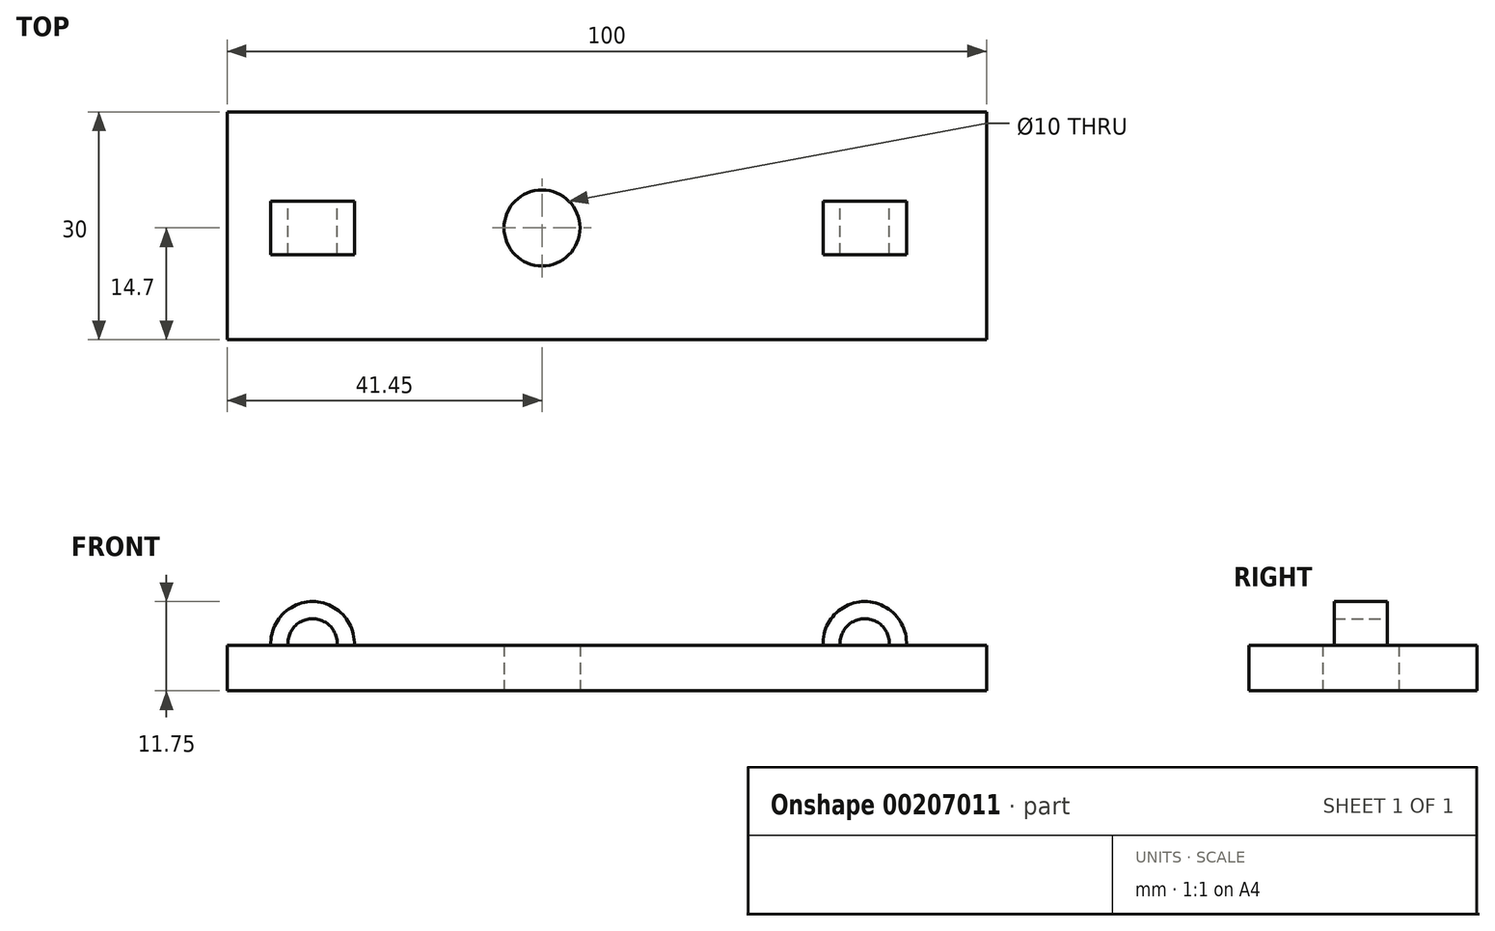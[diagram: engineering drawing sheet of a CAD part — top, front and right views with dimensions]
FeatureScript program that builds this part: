
annotation { "Feature Type Name" : "Feature", "Feature Type Description" : "" }
export const myFeature = defineFeature(function(context is Context, id is Id, definition is map)
    precondition{}
    {
        {
            var Q0;
            Q0=qCreatedBy(makeId("Top.planeOp"),FACE);
            var sketch = newSketch(context, id + "F0", { "sketchPlane" : qUnion([Q0])});
            skLineSegment(sketch, "E0.bottom", {"start": v(-41.45, 15.3) * mm, "end": v(58.55, 15.3) * mm});
            skLineSegment(sketch, "E0.top", {"start": v(-41.45, -14.7) * mm, "end": v(58.55, -14.7) * mm});
            skLineSegment(sketch, "E0.left", {"start": v(-41.45, 15.3) * mm, "end": v(-41.45, -14.7) * mm});
            skLineSegment(sketch, "E0.right", {"start": v(58.55, 15.3) * mm, "end": v(58.55, -14.7) * mm});
            skCircle(sketch, "E1", {"center": v(0, 0) * mm, "radius": 5 * mm});
            skSolve(sketch);
        }
        {
            var Q0;
            Q0=makeQuery(id+"F0.imprint","IMPRINT",FACE,{"disambiguationData":[TD([[makeQuery(id+"F0.imprint","IMPRINT",EDGE,{"derivedFrom":sQuery(id+"F0.wireOp",EDGE,"E0.bottom")}),-1.0]])]});
            var Q1;
            Q1 = qSketchRegion(id + "F0", true);
            extrude(context, id + "F1", {"entities" : qUnion([Q0, Q1]), "depth" : 6 * mm});
        }
        {
            var Q0;
            Q0=qCreatedBy(makeId("Front.planeOp"),FACE);
            var sketch = newSketch(context, id + "F2", { "sketchPlane" : qUnion([Q0])});
            skCircle(sketch, "E2", {"center": v(-30.22, 6.25) * mm, "radius": 5.5 * mm});
            skCircle(sketch, "E3", {"center": v(-30.22, 6.25) * mm, "radius": 3.25 * mm});
            skCircle(sketch, "E4", {"center": v(42.5, 6.25) * mm, "radius": 5.5 * mm});
            skCircle(sketch, "E5", {"center": v(42.5, 6.25) * mm, "radius": 3.25 * mm});
            skSolve(sketch);
        }
        {
            var Q0;
            Q0=makeQuery(id+"F2.imprint","IMPRINT",FACE,{"disambiguationData":[TD([[makeQuery(id+"F2.imprint","IMPRINT",EDGE,{"derivedFrom":sQuery(id+"F2.wireOp",EDGE,"E2")}),1.0]])]});
            var Q1;
            Q1=makeQuery(id+"F2.imprint","IMPRINT",FACE,{"disambiguationData":[TD([[makeQuery(id+"F2.imprint","IMPRINT",EDGE,{"derivedFrom":sQuery(id+"F2.wireOp",EDGE,"E4")}),1.0]])]});
            extrude(context, id + "F3", {"entities" : qUnion([Q0, Q1]), "operationType" : NewBodyOperationType.ADD, "endBound" : BoundingType.SYMMETRIC, "depth" : 7 * mm});
        }
    });
